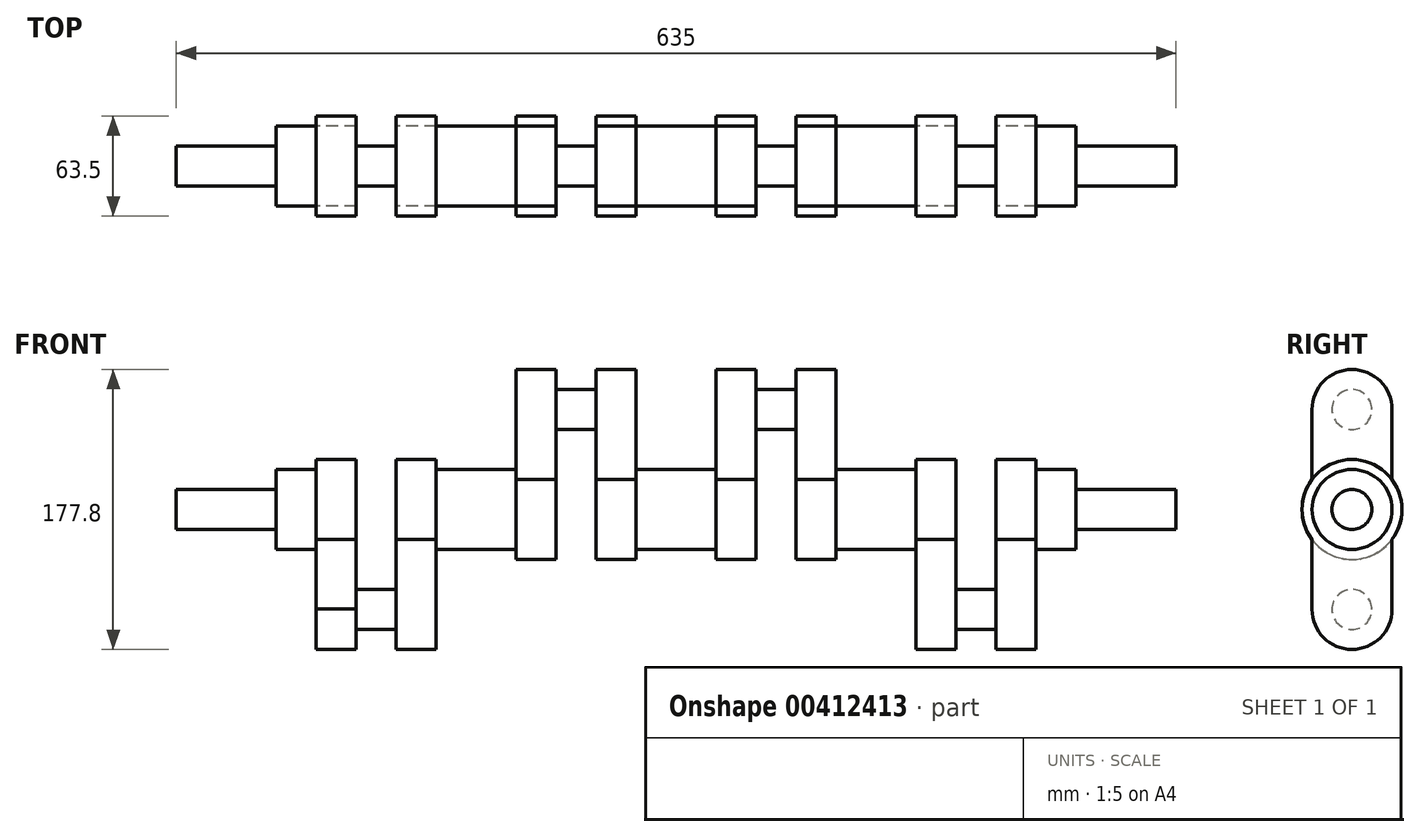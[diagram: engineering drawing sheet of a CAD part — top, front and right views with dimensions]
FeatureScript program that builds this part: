
annotation { "Feature Type Name" : "Feature", "Feature Type Description" : "" }
export const myFeature = defineFeature(function(context is Context, id is Id, definition is map)
    precondition{}
    {
        {
            var Q0;
            Q0=qCreatedBy(makeId("Right.planeOp"),FACE);
            var sketch = newSketch(context, id + "F0", { "sketchPlane" : qUnion([Q0])});
            skCircle(sketch, "E0", {"center": v(0, 0) * mm, "radius": 12.7 * mm});
            skSolve(sketch);
        }
        {
            var Q0;
            Q0 = qSketchRegion(id + "F0", true);
            extrude(context, id + "F1", {"entities" : qUnion([Q0]), "depth" : 63.5 * mm});
        }
        {
            var Q0;
            Q0=makeQuery(id+"F1.opExtrude","CAP_FACE",FACE,{"disambiguationData":[OSD([sQuery(id+"F0.wireOp",EDGE,"E0")])],"isStart":false});
            var sketch = newSketch(context, id + "F2", { "sketchPlane" : qUnion([Q0])});
            skSolve(sketch);
        }
        {
            var Q0;
            Q0=makeQuery(id+"F2.imprint","IMPRINT",FACE,{"disambiguationData":[TD([[makeQuery(id+"F2.imprint","IMPRINT",EDGE,{"derivedFrom":makeQuery(id+"F1.opExtrude","CAP_EDGE",EDGE,{"disambiguationData":[OSD([sQuery(id+"F0.wireOp",EDGE,"E0")])],"isStart":false})}),1.0]])]});
            var sketch = newSketch(context, id + "F3", { "sketchPlane" : qUnion([Q0])});
            skCircle(sketch, "E1", {"center": v(0, 0) * mm, "radius": 25.4 * mm});
            skSolve(sketch);
        }
        {
            var Q0;
            Q0 = qSketchRegion(id + "F3", true);
            extrude(context, id + "F4", {"entities" : qUnion([Q0]), "operationType" : NewBodyOperationType.ADD, "depth" : 25.4 * mm});
        }
        {
            var Q0;
            Q0=makeQuery(id+"F4.opExtrude","CAP_FACE",FACE,{"disambiguationData":[OSD([sQuery(id+"F3.wireOp",EDGE,"E1")])],"isStart":false});
            var sketch = newSketch(context, id + "F5", { "sketchPlane" : qUnion([Q0])});
            skLineSegment(sketch, "E2", {"start": v(-25.4, 0.42) * mm, "end": v(-25.4, -63.08) * mm});
            skLineSegment(sketch, "E3", {"start": v(25.4, -0.42) * mm, "end": v(25.4, -63.92) * mm});
            skLineSegment(sketch, "E4", {"start": v(25.4, -63.92) * mm, "end": v(-25.4, -63.08) * mm});
            skCircle(sketch, "E5", {"center": v(0, 0) * mm, "radius": 31.75 * mm});
            skCircle(sketch, "E6", {"center": v(0, -63.5) * mm, "radius": 25.4 * mm});
            skSolve(sketch);
        }
        {
            var Q0;
            Q0 = qSketchRegion(id + "F5", true);
            extrude(context, id + "F6", {"entities" : qUnion([Q0]), "operationType" : NewBodyOperationType.ADD, "depth" : 25.4 * mm});
        }
        {
            var Q0;
            Q0=makeQuery(id+"F6.opExtrude","CAP_FACE",FACE,{"disambiguationData":[OSD([sQuery(id+"F5.wireOp",EDGE,"E2"),sQuery(id+"F5.wireOp",EDGE,"E3"),sQuery(id+"F5.wireOp",EDGE,"E5"),sQuery(id+"F5.wireOp",EDGE,"E6")])],"isStart":false});
            var sketch = newSketch(context, id + "F7", { "sketchPlane" : qUnion([Q0])});
            skCircle(sketch, "E7", {"center": v(0, -63.5) * mm, "radius": 12.7 * mm});
            skSolve(sketch);
        }
        {
            var Q0;
            Q0 = qSketchRegion(id + "F7", true);
            extrude(context, id + "F8", {"entities" : qUnion([Q0]), "operationType" : NewBodyOperationType.ADD, "depth" : 25.4 * mm});
        }
        {
            var Q0;
            Q0=makeQuery(id+"F8.opExtrude","CAP_FACE",FACE,{"disambiguationData":[OSD([sQuery(id+"F7.wireOp",EDGE,"E7")])],"isStart":false});
            var sketch = newSketch(context, id + "F9", { "sketchPlane" : qUnion([Q0])});
            skCircle(sketch, "E8", {"center": v(0, -63.5) * mm, "radius": 25.4 * mm});
            skLineSegment(sketch, "E9", {"start": v(0, -63.5) * mm, "end": v(25.4, -63.5) * mm});
            skLineSegment(sketch, "E10", {"start": v(25.4, -63.5) * mm, "end": v(-25.4, -63.5) * mm});
            skLineSegment(sketch, "E11", {"start": v(-25.4, -63.5) * mm, "end": v(-25.4, 0) * mm});
            skLineSegment(sketch, "E12", {"start": v(25.4, -63.5) * mm, "end": v(25.4, 0) * mm});
            skCircle(sketch, "E13", {"center": v(0, 0) * mm, "radius": 25.4 * mm});
            skCircle(sketch, "E14", {"center": v(0, 0) * mm, "radius": 31.75 * mm});
            skSolve(sketch);
        }
        {
            var Q0;
            Q0 = qSketchRegion(id + "F9", true);
            var Q1;
            {var subQ0=sQuery(id+"F9.wireOp",EDGE,"E13");var subQ1=makeQuery(id+"F9.imprint","INTERSECT",VERTEX,{"derivedFrom":[sQuery(id+"F9.wireOp",EDGE,"E11"),subQ0]});Q1=makeQuery(id+"F9.imprint","IMPRINT",FACE,{"disambiguationData":[TD([[makeQuery(id+"F9.imprint","IMPRINT",EDGE,{"disambiguationData":[TD([[subQ1,1.0]])],"derivedFrom":subQ0}),1.0]])]});}
            extrude(context, id + "F10", {"entities" : qUnion([Q0, Q1]), "operationType" : NewBodyOperationType.ADD, "depth" : 25.4 * mm});
        }
        {
            var Q0;
            Q0=makeQuery(id+"F10.opExtrude","CAP_FACE",FACE,{"disambiguationData":[OSD([sQuery(id+"F9.wireOp",EDGE,"E8"),sQuery(id+"F9.wireOp",EDGE,"E11"),sQuery(id+"F9.wireOp",EDGE,"E12"),sQuery(id+"F9.wireOp",EDGE,"E14")])],"isStart":false});
            var sketch = newSketch(context, id + "F11", { "sketchPlane" : qUnion([Q0])});
            skCircle(sketch, "E15", {"center": v(0, 0) * mm, "radius": 25.4 * mm});
            skSolve(sketch);
        }
        {
            var Q0;
            Q0 = qSketchRegion(id + "F11", true);
            extrude(context, id + "F12", {"entities" : qUnion([Q0]), "operationType" : NewBodyOperationType.ADD, "depth" : 50.8 * mm});
        }
        {
            var Q0;
            Q0=makeQuery(id+"F12.opExtrude","CAP_FACE",FACE,{"disambiguationData":[OSD([sQuery(id+"F11.wireOp",EDGE,"E15")])],"isStart":false});
            var sketch = newSketch(context, id + "F13", { "sketchPlane" : qUnion([Q0])});
            skCircle(sketch, "E16", {"center": v(0, 0) * mm, "radius": 25.4 * mm});
            skLineSegment(sketch, "E17", {"start": v(0, 0) * mm, "end": v(25.4, 0) * mm});
            skLineSegment(sketch, "E18", {"start": v(25.4, 0) * mm, "end": v(-25.4, 0) * mm});
            skLineSegment(sketch, "E19", {"start": v(-25.4, 0) * mm, "end": v(-25.4, 63.5) * mm});
            skLineSegment(sketch, "E20", {"start": v(25.4, 63.5) * mm, "end": v(25.4, 0) * mm});
            skLineSegment(sketch, "E21", {"start": v(-25.4, 63.5) * mm, "end": v(25.4, 63.5) * mm});
            skCircle(sketch, "E22", {"center": v(0, 63.5) * mm, "radius": 25.4 * mm});
            skCircle(sketch, "E23", {"center": v(0, 0) * mm, "radius": 31.75 * mm});
            skSolve(sketch);
        }
        {
            var Q0;
            {var subQ0=sQuery(id+"F13.wireOp",EDGE,"E18");var subQ4=makeQuery(id+"F13.imprint","IMPRINT",VERTEX,{"derivedFrom":subQ0});Q0=makeQuery(id+"F13.imprint","IMPRINT",FACE,{"disambiguationData":[TD([[makeQuery(id+"F13.imprint","IMPRINT",EDGE,{"disambiguationData":[TD([[subQ4,1.0]])],"derivedFrom":subQ0}),1.0]])]});}
            var Q1;
            {var subQ0=sQuery(id+"F13.wireOp",EDGE,"E21");Q1=makeQuery(id+"F13.imprint","IMPRINT",FACE,{"disambiguationData":[TD([[makeQuery(id+"F13.imprint","IMPRINT",EDGE,{"derivedFrom":subQ0}),1.0]])]});}
            var Q2;
            {var subQ0=sQuery(id+"F13.wireOp",EDGE,"E18");var subQ4=makeQuery(id+"F13.imprint","IMPRINT",VERTEX,{"derivedFrom":subQ0});Q2=makeQuery(id+"F13.imprint","IMPRINT",FACE,{"disambiguationData":[TD([[makeQuery(id+"F13.imprint","IMPRINT",EDGE,{"disambiguationData":[TD([[subQ4,1.0]])],"derivedFrom":subQ0}),-1.0]])]});}
            var Q3;
            {var subQ0=sQuery(id+"F13.wireOp",EDGE,"E21");Q3=makeQuery(id+"F13.imprint","IMPRINT",FACE,{"disambiguationData":[TD([[makeQuery(id+"F13.imprint","IMPRINT",EDGE,{"derivedFrom":subQ0}),-1.0]])]});}
            var Q4;
            {var subQ4=sQuery(id+"F13.wireOp",EDGE,"E19");var subQ6=sQuery(id+"F13.wireOp",EDGE,"E23");var subQ7=makeQuery(id+"F13.imprint","INTERSECT",VERTEX,{"derivedFrom":[subQ4,subQ6]});Q4=makeQuery(id+"F13.imprint","IMPRINT",FACE,{"disambiguationData":[TD([[makeQuery(id+"F13.imprint","IMPRINT",EDGE,{"disambiguationData":[TD([[subQ7,-1.0]])],"derivedFrom":subQ6}),1.0]])]});}
            var Q5;
            {var subQ4=sQuery(id+"F13.wireOp",EDGE,"E19");var subQ6=sQuery(id+"F13.wireOp",EDGE,"E23");var subQ7=makeQuery(id+"F13.imprint","INTERSECT",VERTEX,{"derivedFrom":[subQ4,subQ6]});Q5=makeQuery(id+"F13.imprint","IMPRINT",FACE,{"disambiguationData":[TD([[makeQuery(id+"F13.imprint","IMPRINT",EDGE,{"disambiguationData":[TD([[subQ7,1.0]])],"derivedFrom":subQ6}),1.0]])]});}
            var Q6;
            {var subQ2=sQuery(id+"F13.wireOp",EDGE,"E19");var subQ4=sQuery(id+"F13.wireOp",EDGE,"E23");var subQ5=makeQuery(id+"F13.imprint","INTERSECT",VERTEX,{"derivedFrom":[subQ2,subQ4]});Q6=makeQuery(id+"F13.imprint","IMPRINT",FACE,{"disambiguationData":[TD([[makeQuery(id+"F13.imprint","IMPRINT",EDGE,{"disambiguationData":[TD([[subQ5,1.0]])],"derivedFrom":subQ4}),-1.0]])]});}
            extrude(context, id + "F14", {"entities" : qUnion([Q0, Q1, Q2, Q3, Q4, Q5, Q6]), "operationType" : NewBodyOperationType.ADD, "depth" : 25.4 * mm});
        }
        {
            var Q0;
            Q0=makeQuery(id+"F14.opExtrude","CAP_FACE",FACE,{"disambiguationData":[OSD([sQuery(id+"F13.wireOp",EDGE,"E19"),sQuery(id+"F13.wireOp",EDGE,"E20"),sQuery(id+"F13.wireOp",EDGE,"E22"),sQuery(id+"F13.wireOp",EDGE,"E23")])],"isStart":false});
            var sketch = newSketch(context, id + "F15", { "sketchPlane" : qUnion([Q0])});
            skCircle(sketch, "E24", {"center": v(0, 63.5) * mm, "radius": 12.7 * mm});
            skSolve(sketch);
        }
        {
            var Q0;
            Q0 = qSketchRegion(id + "F15", true);
            extrude(context, id + "F16", {"entities" : qUnion([Q0]), "operationType" : NewBodyOperationType.ADD, "depth" : 25.4 * mm});
        }
        {
            var Q0;
            Q0=makeQuery(id+"F16.opExtrude","CAP_FACE",FACE,{"disambiguationData":[OSD([sQuery(id+"F15.wireOp",EDGE,"E24")])],"isStart":false});
            var sketch = newSketch(context, id + "F17", { "sketchPlane" : qUnion([Q0])});
            skCircle(sketch, "E25", {"center": v(0, 63.5) * mm, "radius": 25.4 * mm});
            skLineSegment(sketch, "E26", {"start": v(25.4, 63.5) * mm, "end": v(-25.4, 63.5) * mm});
            skLineSegment(sketch, "E27", {"start": v(-25.4, 63.5) * mm, "end": v(-25.4, 0) * mm});
            skLineSegment(sketch, "E28", {"start": v(25.4, 0) * mm, "end": v(25.4, 63.5) * mm});
            skCircle(sketch, "E29", {"center": v(0, 0) * mm, "radius": 25.4 * mm});
            skCircle(sketch, "E30", {"center": v(0, 0) * mm, "radius": 31.75 * mm});
            skSolve(sketch);
        }
        {
            var Q0;
            Q0 = qSketchRegion(id + "F17", true);
            var Q1;
            {var subQ0=sQuery(id+"F17.wireOp",EDGE,"E29");var subQ1=makeQuery(id+"F17.imprint","INTERSECT",VERTEX,{"derivedFrom":[sQuery(id+"F17.wireOp",EDGE,"E27"),subQ0]});Q1=makeQuery(id+"F17.imprint","IMPRINT",FACE,{"disambiguationData":[TD([[makeQuery(id+"F17.imprint","IMPRINT",EDGE,{"disambiguationData":[TD([[subQ1,1.0]])],"derivedFrom":subQ0}),1.0]])]});}
            extrude(context, id + "F18", {"entities" : qUnion([Q0, Q1]), "operationType" : NewBodyOperationType.ADD, "depth" : 25.4 * mm});
        }
        {
            var Q0;
            Q0=makeQuery(id+"F18.opExtrude","CAP_FACE",FACE,{"disambiguationData":[OSD([sQuery(id+"F17.wireOp",EDGE,"E25"),sQuery(id+"F17.wireOp",EDGE,"E27"),sQuery(id+"F17.wireOp",EDGE,"E28"),sQuery(id+"F17.wireOp",EDGE,"E30")])],"isStart":false});
            var sketch = newSketch(context, id + "F19", { "sketchPlane" : qUnion([Q0])});
            skCircle(sketch, "E31", {"center": v(0, 0) * mm, "radius": 25.4 * mm});
            skSolve(sketch);
        }
        {
            var Q0;
            Q0 = qSketchRegion(id + "F19", true);
            extrude(context, id + "F20", {"entities" : qUnion([Q0]), "operationType" : NewBodyOperationType.ADD, "depth" : 50.8 * mm});
        }
        {
            var Q0;
            Q0=makeQuery(id+"F20.opExtrude","CAP_FACE",FACE,{"disambiguationData":[OSD([sQuery(id+"F19.wireOp",EDGE,"E31")])],"isStart":false});
            var sketch = newSketch(context, id + "F21", { "sketchPlane" : qUnion([Q0])});
            skCircle(sketch, "E32", {"center": v(0, 0) * mm, "radius": 31.75 * mm});
            skCircle(sketch, "E33", {"center": v(0, 0) * mm, "radius": 25.4 * mm});
            skLineSegment(sketch, "E34", {"start": v(25.4, 0) * mm, "end": v(-25.4, 0) * mm});
            skLineSegment(sketch, "E35", {"start": v(-25.4, 0) * mm, "end": v(-25.4, 63.5) * mm});
            skLineSegment(sketch, "E36", {"start": v(25.4, 0) * mm, "end": v(25.4, 63.5) * mm});
            skLineSegment(sketch, "E37", {"start": v(-25.4, 63.5) * mm, "end": v(25.4, 63.5) * mm});
            skCircle(sketch, "E38", {"center": v(0, 63.5) * mm, "radius": 25.4 * mm});
            skSolve(sketch);
        }
        {
            var Q0;
            {var subQ0=sQuery(id+"F21.wireOp",EDGE,"E34");Q0=makeQuery(id+"F21.imprint","IMPRINT",FACE,{"disambiguationData":[TD([[makeQuery(id+"F21.imprint","IMPRINT",EDGE,{"derivedFrom":subQ0}),-1.0]])]});}
            var Q1;
            {var subQ0=sQuery(id+"F21.wireOp",EDGE,"E37");Q1=makeQuery(id+"F21.imprint","IMPRINT",FACE,{"disambiguationData":[TD([[makeQuery(id+"F21.imprint","IMPRINT",EDGE,{"derivedFrom":subQ0}),-1.0]])]});}
            var Q2;
            {var subQ0=sQuery(id+"F21.wireOp",EDGE,"E35");var subQ1=sQuery(id+"F21.wireOp",EDGE,"E32");var subQ2=makeQuery(id+"F21.imprint","INTERSECT",VERTEX,{"derivedFrom":[subQ1,subQ0]});Q2=makeQuery(id+"F21.imprint","IMPRINT",FACE,{"disambiguationData":[TD([[makeQuery(id+"F21.imprint","IMPRINT",EDGE,{"disambiguationData":[TD([[subQ2,1.0]])],"derivedFrom":subQ1}),1.0]])]});}
            var Q3;
            {var subQ0=sQuery(id+"F21.wireOp",EDGE,"E35");var subQ1=sQuery(id+"F21.wireOp",EDGE,"E32");var subQ2=makeQuery(id+"F21.imprint","INTERSECT",VERTEX,{"derivedFrom":[subQ1,subQ0]});Q3=makeQuery(id+"F21.imprint","IMPRINT",FACE,{"disambiguationData":[TD([[makeQuery(id+"F21.imprint","IMPRINT",EDGE,{"disambiguationData":[TD([[subQ2,-1.0]])],"derivedFrom":subQ1}),1.0]])]});}
            var Q4;
            {var subQ0=sQuery(id+"F21.wireOp",EDGE,"E37");Q4=makeQuery(id+"F21.imprint","IMPRINT",FACE,{"disambiguationData":[TD([[makeQuery(id+"F21.imprint","IMPRINT",EDGE,{"derivedFrom":subQ0}),1.0]])]});}
            var Q5;
            {var subQ0=sQuery(id+"F21.wireOp",EDGE,"E35");var subQ1=sQuery(id+"F21.wireOp",EDGE,"E32");var subQ2=makeQuery(id+"F21.imprint","INTERSECT",VERTEX,{"derivedFrom":[subQ1,subQ0]});Q5=makeQuery(id+"F21.imprint","IMPRINT",FACE,{"disambiguationData":[TD([[makeQuery(id+"F21.imprint","IMPRINT",EDGE,{"disambiguationData":[TD([[subQ2,1.0]])],"derivedFrom":subQ1}),-1.0]])]});}
            var Q6;
            {var subQ0=sQuery(id+"F21.wireOp",EDGE,"E34");Q6=makeQuery(id+"F21.imprint","IMPRINT",FACE,{"disambiguationData":[TD([[makeQuery(id+"F21.imprint","IMPRINT",EDGE,{"derivedFrom":subQ0}),1.0]])]});}
            extrude(context, id + "F22", {"entities" : qUnion([Q0, Q1, Q2, Q3, Q4, Q5, Q6]), "operationType" : NewBodyOperationType.ADD, "depth" : 25.4 * mm});
        }
        {
            var Q0;
            Q0=makeQuery(id+"F22.opExtrude","CAP_FACE",FACE,{"disambiguationData":[OSD([sQuery(id+"F21.wireOp",EDGE,"E32"),sQuery(id+"F21.wireOp",EDGE,"E35"),sQuery(id+"F21.wireOp",EDGE,"E36"),sQuery(id+"F21.wireOp",EDGE,"E38")])],"isStart":false});
            var sketch = newSketch(context, id + "F23", { "sketchPlane" : qUnion([Q0])});
            skCircle(sketch, "E39", {"center": v(0, 63.5) * mm, "radius": 12.7 * mm});
            skSolve(sketch);
        }
        {
            var Q0;
            Q0 = qSketchRegion(id + "F23", true);
            extrude(context, id + "F24", {"entities" : qUnion([Q0]), "operationType" : NewBodyOperationType.ADD, "depth" : 25.4 * mm});
        }
        {
            var Q0;
            Q0=makeQuery(id+"F24.opExtrude","CAP_FACE",FACE,{"disambiguationData":[OSD([sQuery(id+"F23.wireOp",EDGE,"E39")])],"isStart":false});
            var sketch = newSketch(context, id + "F25", { "sketchPlane" : qUnion([Q0])});
            skCircle(sketch, "E40", {"center": v(0, 63.5) * mm, "radius": 25.4 * mm});
            skLineSegment(sketch, "E41", {"start": v(0, 63.5) * mm, "end": v(25.4, 63.5) * mm});
            skLineSegment(sketch, "E42", {"start": v(25.4, 63.5) * mm, "end": v(-25.4, 63.5) * mm});
            skLineSegment(sketch, "E43", {"start": v(-25.4, 0) * mm, "end": v(-25.4, 63.5) * mm});
            skLineSegment(sketch, "E44", {"start": v(25.4, 0) * mm, "end": v(25.4, 63.5) * mm});
            skLineSegment(sketch, "E45", {"start": v(25.4, 0) * mm, "end": v(-25.4, 0) * mm});
            skCircle(sketch, "E46", {"center": v(0, 0) * mm, "radius": 31.75 * mm});
            skSolve(sketch);
        }
        {
            var Q0;
            Q0 = qSketchRegion(id + "F25", true);
            extrude(context, id + "F26", {"entities" : qUnion([Q0]), "operationType" : NewBodyOperationType.ADD, "depth" : 25.4 * mm});
        }
        {
            var Q0;
            Q0=makeQuery(id+"F26.opExtrude","CAP_FACE",FACE,{"disambiguationData":[OSD([sQuery(id+"F25.wireOp",EDGE,"E40"),sQuery(id+"F25.wireOp",EDGE,"E43"),sQuery(id+"F25.wireOp",EDGE,"E44"),sQuery(id+"F25.wireOp",EDGE,"E46")])],"isStart":false});
            var sketch = newSketch(context, id + "F27", { "sketchPlane" : qUnion([Q0])});
            skCircle(sketch, "E47", {"center": v(0, 0) * mm, "radius": 25.4 * mm});
            skSolve(sketch);
        }
        {
            var Q0;
            Q0 = qSketchRegion(id + "F27", true);
            extrude(context, id + "F28", {"entities" : qUnion([Q0]), "operationType" : NewBodyOperationType.ADD, "depth" : 50.8 * mm});
        }
        {
            var Q0;
            Q0=makeQuery(id+"F28.opExtrude","CAP_FACE",FACE,{"disambiguationData":[OSD([sQuery(id+"F27.wireOp",EDGE,"E47")])],"isStart":false});
            var sketch = newSketch(context, id + "F29", { "sketchPlane" : qUnion([Q0])});
            skCircle(sketch, "E48", {"center": v(0, 0) * mm, "radius": 31.75 * mm});
            skCircle(sketch, "E49", {"center": v(0, 0) * mm, "radius": 25.4 * mm});
            skLineSegment(sketch, "E50", {"start": v(25.4, 0) * mm, "end": v(-25.4, 0) * mm});
            skLineSegment(sketch, "E51", {"start": v(-25.4, 0) * mm, "end": v(-25.4, -63.5) * mm});
            skLineSegment(sketch, "E52", {"start": v(25.4, 0) * mm, "end": v(25.4, -63.5) * mm});
            skLineSegment(sketch, "E53", {"start": v(25.4, -63.5) * mm, "end": v(-25.4, -63.5) * mm});
            skCircle(sketch, "E54", {"center": v(0, -63.5) * mm, "radius": 25.4 * mm});
            skSolve(sketch);
        }
        {
            var Q0;
            Q0 = qSketchRegion(id + "F29", true);
            var Q1;
            {var subQ0=sQuery(id+"F29.wireOp",EDGE,"E50");Q1=makeQuery(id+"F29.imprint","IMPRINT",FACE,{"disambiguationData":[TD([[makeQuery(id+"F29.imprint","IMPRINT",EDGE,{"derivedFrom":subQ0}),-1.0]])]});}
            var Q2;
            {var subQ0=sQuery(id+"F29.wireOp",EDGE,"E50");Q2=makeQuery(id+"F29.imprint","IMPRINT",FACE,{"disambiguationData":[TD([[makeQuery(id+"F29.imprint","IMPRINT",EDGE,{"derivedFrom":subQ0}),1.0]])]});}
            extrude(context, id + "F30", {"entities" : qUnion([Q0, Q1, Q2]), "operationType" : NewBodyOperationType.ADD, "depth" : 25.4 * mm});
        }
        {
            var Q0;
            Q0=makeQuery(id+"F30.opExtrude","CAP_FACE",FACE,{"disambiguationData":[OSD([sQuery(id+"F29.wireOp",EDGE,"E48"),sQuery(id+"F29.wireOp",EDGE,"E51"),sQuery(id+"F29.wireOp",EDGE,"E52"),sQuery(id+"F29.wireOp",EDGE,"E54")])],"isStart":false});
            var sketch = newSketch(context, id + "F31", { "sketchPlane" : qUnion([Q0])});
            skCircle(sketch, "E55", {"center": v(0, -63.5) * mm, "radius": 12.7 * mm});
            skSolve(sketch);
        }
        {
            var Q0;
            Q0 = qSketchRegion(id + "F31", true);
            extrude(context, id + "F32", {"entities" : qUnion([Q0]), "operationType" : NewBodyOperationType.ADD, "depth" : 25.4 * mm});
        }
        {
            var Q0;
            Q0=makeQuery(id+"F32.opExtrude","CAP_FACE",FACE,{"disambiguationData":[OSD([sQuery(id+"F31.wireOp",EDGE,"E55")])],"isStart":false});
            var sketch = newSketch(context, id + "F33", { "sketchPlane" : qUnion([Q0])});
            skCircle(sketch, "E56", {"center": v(0, -63.5) * mm, "radius": 25.4 * mm});
            skLineSegment(sketch, "E57", {"start": v(0, -63.5) * mm, "end": v(25.4, -63.5) * mm});
            skLineSegment(sketch, "E58", {"start": v(25.4, -63.5) * mm, "end": v(-25.4, -63.5) * mm});
            skCircle(sketch, "E59", {"center": v(0, 0) * mm, "radius": 25.4 * mm});
            skLineSegment(sketch, "E60", {"start": v(0, 0) * mm, "end": v(25.4, 0) * mm});
            skLineSegment(sketch, "E61", {"start": v(25.4, 0) * mm, "end": v(-25.4, 0) * mm});
            skLineSegment(sketch, "E62", {"start": v(-25.4, 0) * mm, "end": v(-25.4, -63.5) * mm});
            skLineSegment(sketch, "E63", {"start": v(25.4, -63.5) * mm, "end": v(25.4, 0) * mm});
            skCircle(sketch, "E64", {"center": v(0, 0) * mm, "radius": 31.75 * mm});
            skSolve(sketch);
        }
        {
            var Q0;
            Q0 = qSketchRegion(id + "F33", true);
            var Q1;
            {var subQ0=sQuery(id+"F33.wireOp",EDGE,"E61");var subQ4=makeQuery(id+"F33.imprint","IMPRINT",VERTEX,{"derivedFrom":subQ0});Q1=makeQuery(id+"F33.imprint","IMPRINT",FACE,{"disambiguationData":[TD([[makeQuery(id+"F33.imprint","IMPRINT",EDGE,{"disambiguationData":[TD([[subQ4,1.0]])],"derivedFrom":subQ0}),-1.0]])]});}
            var Q2;
            {var subQ0=sQuery(id+"F33.wireOp",EDGE,"E61");var subQ4=makeQuery(id+"F33.imprint","IMPRINT",VERTEX,{"derivedFrom":subQ0});Q2=makeQuery(id+"F33.imprint","IMPRINT",FACE,{"disambiguationData":[TD([[makeQuery(id+"F33.imprint","IMPRINT",EDGE,{"disambiguationData":[TD([[subQ4,1.0]])],"derivedFrom":subQ0}),1.0]])]});}
            extrude(context, id + "F34", {"entities" : qUnion([Q0, Q1, Q2]), "operationType" : NewBodyOperationType.ADD, "depth" : 25.4 * mm});
        }
        {
            var Q0;
            Q0=makeQuery(id+"F34.opExtrude","CAP_FACE",FACE,{"disambiguationData":[OSD([sQuery(id+"F33.wireOp",EDGE,"E56"),sQuery(id+"F33.wireOp",EDGE,"E62"),sQuery(id+"F33.wireOp",EDGE,"E63"),sQuery(id+"F33.wireOp",EDGE,"E64")])],"isStart":false});
            var sketch = newSketch(context, id + "F35", { "sketchPlane" : qUnion([Q0])});
            skCircle(sketch, "E65", {"center": v(0, 0) * mm, "radius": 25.4 * mm});
            skSolve(sketch);
        }
        {
            var Q0;
            Q0 = qSketchRegion(id + "F35", true);
            extrude(context, id + "F36", {"entities" : qUnion([Q0]), "operationType" : NewBodyOperationType.ADD, "depth" : 25.4 * mm});
        }
        {
            var Q0;
            Q0=makeQuery(id+"F36.opExtrude","CAP_FACE",FACE,{"disambiguationData":[OSD([sQuery(id+"F35.wireOp",EDGE,"E65")])],"isStart":false});
            var sketch = newSketch(context, id + "F37", { "sketchPlane" : qUnion([Q0])});
            skCircle(sketch, "E66", {"center": v(0, 0) * mm, "radius": 12.7 * mm});
            skSolve(sketch);
        }
        {
            var Q0;
            Q0 = qSketchRegion(id + "F37", true);
            extrude(context, id + "F38", {"entities" : qUnion([Q0]), "operationType" : NewBodyOperationType.ADD, "depth" : 63.5 * mm});
        }
    });
